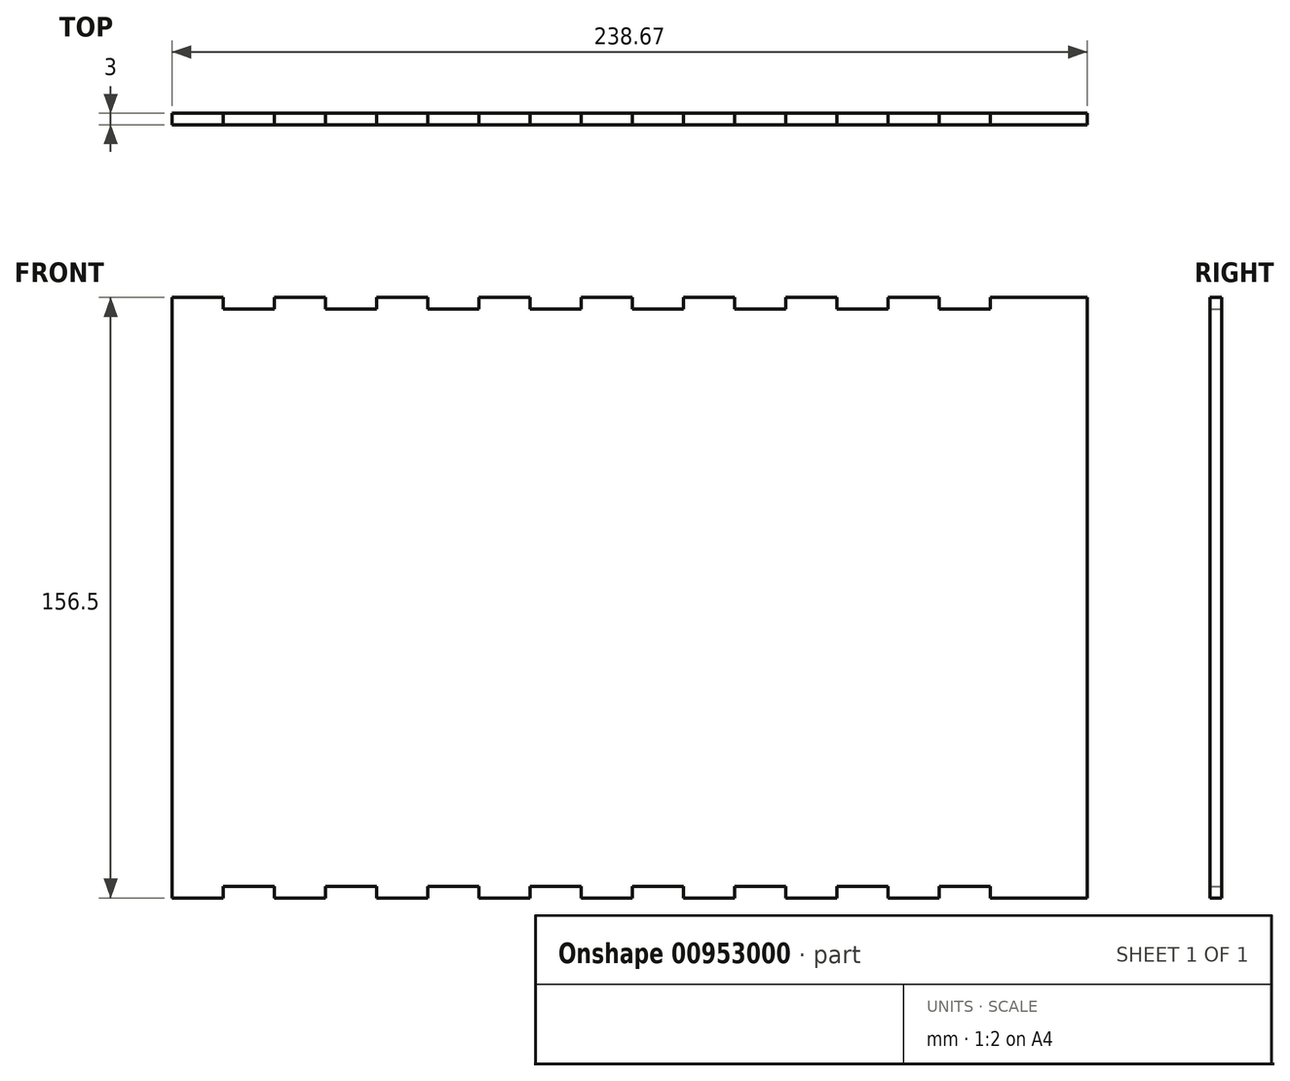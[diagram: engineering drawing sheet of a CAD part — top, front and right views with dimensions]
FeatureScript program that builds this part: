
annotation { "Feature Type Name" : "Feature", "Feature Type Description" : "" }
export const myFeature = defineFeature(function(context is Context, id is Id, definition is map)
    precondition{}
    {
        {
            var Q0;
            Q0=qCreatedBy(makeId("Front.planeOp"),FACE);
            var sketch = newSketch(context, id + "F0", { "sketchPlane" : qUnion([Q0])});
            skPoint(sketch, "E0.middle", {"position": v(-0.98, 0.74) * mm});
            skLineSegment(sketch, "E1", {"start": v(-87.73, 79.24) * mm, "end": v(-74.4, 79.24) * mm});
            skLineSegment(sketch, "E2", {"start": v(-87.73, 82.24) * mm, "end": v(-87.73, 79.24) * mm});
            skLineSegment(sketch, "E3", {"start": v(-74.4, 82.24) * mm, "end": v(-74.4, 79.24) * mm});
            skLineSegment(sketch, "E4", {"start": v(-61.06, 82.24) * mm, "end": v(-61.06, 79.24) * mm});
            skLineSegment(sketch, "E5", {"start": v(-47.73, 82.24) * mm, "end": v(-47.73, 79.24) * mm});
            skLineSegment(sketch, "E6", {"start": v(-34.4, 82.24) * mm, "end": v(-34.4, 79.24) * mm});
            skLineSegment(sketch, "E7", {"start": v(-21.06, 82.24) * mm, "end": v(-21.06, 79.24) * mm});
            skLineSegment(sketch, "E8", {"start": v(-7.73, 82.24) * mm, "end": v(-7.73, 79.24) * mm});
            skLineSegment(sketch, "E9", {"start": v(5.6, 82.24) * mm, "end": v(5.6, 79.24) * mm});
            skLineSegment(sketch, "E10", {"start": v(18.94, 82.24) * mm, "end": v(18.94, 79.24) * mm});
            skLineSegment(sketch, "E11", {"start": v(32.27, 82.24) * mm, "end": v(32.27, 79.24) * mm});
            skLineSegment(sketch, "E12", {"start": v(45.6, 82.24) * mm, "end": v(45.6, 79.24) * mm});
            skLineSegment(sketch, "E13", {"start": v(58.94, 82.24) * mm, "end": v(58.94, 79.24) * mm});
            skLineSegment(sketch, "E14", {"start": v(72.27, 82.24) * mm, "end": v(72.27, 79.24) * mm});
            skLineSegment(sketch, "E15", {"start": v(85.6, 82.24) * mm, "end": v(85.6, 79.24) * mm});
            skLineSegment(sketch, "E16.trimOffspring", {"start": v(-87.73, 82.24) * mm, "end": v(-101.06, 82.24) * mm});
            skLineSegment(sketch, "E17.trimOffspring", {"start": v(-61.06, 79.24) * mm, "end": v(-47.73, 79.24) * mm});
            skLineSegment(sketch, "E18.trimOffspring", {"start": v(-61.06, 82.24) * mm, "end": v(-74.4, 82.24) * mm});
            skLineSegment(sketch, "E19.trimOffspring", {"start": v(-34.4, 79.24) * mm, "end": v(-21.06, 79.24) * mm});
            skLineSegment(sketch, "E20.trimOffspring", {"start": v(-34.4, 82.24) * mm, "end": v(-47.73, 82.24) * mm});
            skLineSegment(sketch, "E21.trimOffspring", {"start": v(-7.73, 79.24) * mm, "end": v(5.6, 79.24) * mm});
            skLineSegment(sketch, "E22.trimOffspring", {"start": v(-7.73, 82.24) * mm, "end": v(-21.06, 82.24) * mm});
            skLineSegment(sketch, "E23.trimOffspring", {"start": v(18.94, 79.24) * mm, "end": v(32.27, 79.24) * mm});
            skLineSegment(sketch, "E24.trimOffspring", {"start": v(18.94, 82.24) * mm, "end": v(5.6, 82.24) * mm});
            skLineSegment(sketch, "E25.trimOffspring", {"start": v(45.6, 79.24) * mm, "end": v(58.94, 79.24) * mm});
            skLineSegment(sketch, "E26.trimOffspring", {"start": v(45.6, 82.24) * mm, "end": v(32.27, 82.24) * mm});
            skLineSegment(sketch, "E27.trimOffspring", {"start": v(72.27, 79.24) * mm, "end": v(85.6, 79.24) * mm});
            skLineSegment(sketch, "E28.trimOffspring", {"start": v(72.27, 82.24) * mm, "end": v(58.94, 82.24) * mm});
            skLineSegment(sketch, "E29", {"start": v(85.6, 82.24) * mm, "end": v(110.94, 82.24) * mm});
            skLineSegment(sketch, "E30", {"start": v(-114.4, 79.24) * mm, "end": v(-101.06, 79.24) * mm});
            skLineSegment(sketch, "E31", {"start": v(-114.4, 82.24) * mm, "end": v(-114.4, 79.24) * mm});
            skLineSegment(sketch, "E32.trimOffspring", {"start": v(-114.4, 82.24) * mm, "end": v(-127.73, 82.24) * mm});
            skLineSegment(sketch, "E33.MirrorCS", {"start": v(-114.4, -74.26) * mm, "end": v(-114.4, -71.26) * mm});
            skLineSegment(sketch, "E34.MirrorCS", {"start": v(-101.06, -74.26) * mm, "end": v(-101.06, -71.26) * mm});
            skLineSegment(sketch, "E35.MirrorCS", {"start": v(-61.06, -74.26) * mm, "end": v(-61.06, -71.26) * mm});
            skLineSegment(sketch, "E36.MirrorCS", {"start": v(32.27, -74.26) * mm, "end": v(32.27, -71.26) * mm});
            skLineSegment(sketch, "E37.MirrorCS", {"start": v(-74.4, -74.26) * mm, "end": v(-74.4, -71.26) * mm});
            skLineSegment(sketch, "E38.MirrorCS", {"start": v(-87.73, -74.26) * mm, "end": v(-87.73, -71.26) * mm});
            skLineSegment(sketch, "E39.MirrorCS", {"start": v(-21.06, -74.26) * mm, "end": v(-21.06, -71.26) * mm});
            skLineSegment(sketch, "E40.MirrorCS", {"start": v(45.6, -74.26) * mm, "end": v(45.6, -71.26) * mm});
            skLineSegment(sketch, "E41.MirrorCS", {"start": v(72.27, -74.26) * mm, "end": v(72.27, -71.26) * mm});
            skLineSegment(sketch, "E42.MirrorCS", {"start": v(85.6, -74.26) * mm, "end": v(85.6, -71.26) * mm});
            skLineSegment(sketch, "E43.MirrorCS", {"start": v(-7.73, -74.26) * mm, "end": v(-7.73, -71.26) * mm});
            skLineSegment(sketch, "E44.MirrorCS", {"start": v(-34.4, -74.26) * mm, "end": v(-34.4, -71.26) * mm});
            skLineSegment(sketch, "E45.MirrorCS", {"start": v(58.94, -74.26) * mm, "end": v(58.94, -71.26) * mm});
            skLineSegment(sketch, "E46.MirrorCS", {"start": v(5.6, -74.26) * mm, "end": v(5.6, -71.26) * mm});
            skLineSegment(sketch, "E47.MirrorCS", {"start": v(-47.73, -74.26) * mm, "end": v(-47.73, -71.26) * mm});
            skLineSegment(sketch, "E48.MirrorCS", {"start": v(18.94, -74.26) * mm, "end": v(18.94, -71.26) * mm});
            skLineSegment(sketch, "E49.MirrorCS", {"start": v(-114.4, -74.26) * mm, "end": v(-127.73, -74.26) * mm});
            skLineSegment(sketch, "E50.MirrorCS", {"start": v(-114.4, -71.26) * mm, "end": v(-101.06, -71.26) * mm});
            skLineSegment(sketch, "E51.MirrorCS", {"start": v(-7.73, -71.26) * mm, "end": v(5.6, -71.26) * mm});
            skLineSegment(sketch, "E52.MirrorCS", {"start": v(45.6, -74.26) * mm, "end": v(32.27, -74.26) * mm});
            skLineSegment(sketch, "E53.MirrorCS", {"start": v(72.27, -71.26) * mm, "end": v(85.6, -71.26) * mm});
            skLineSegment(sketch, "E54.MirrorCS", {"start": v(85.6, -74.26) * mm, "end": v(110.94, -74.26) * mm});
            skLineSegment(sketch, "E55.MirrorCS", {"start": v(-7.73, -74.26) * mm, "end": v(-21.06, -74.26) * mm});
            skLineSegment(sketch, "E56.MirrorCS", {"start": v(72.27, -74.26) * mm, "end": v(58.94, -74.26) * mm});
            skLineSegment(sketch, "E57.MirrorCS", {"start": v(-34.4, -74.26) * mm, "end": v(-47.73, -74.26) * mm});
            skLineSegment(sketch, "E58.MirrorCS", {"start": v(-61.06, -71.26) * mm, "end": v(-47.73, -71.26) * mm});
            skLineSegment(sketch, "E59.MirrorCS", {"start": v(18.94, -74.26) * mm, "end": v(5.6, -74.26) * mm});
            skLineSegment(sketch, "E60.MirrorCS", {"start": v(-34.4, -71.26) * mm, "end": v(-21.06, -71.26) * mm});
            skLineSegment(sketch, "E61.MirrorCS", {"start": v(-87.73, -71.26) * mm, "end": v(-74.4, -71.26) * mm});
            skLineSegment(sketch, "E62.MirrorCS", {"start": v(18.94, -71.26) * mm, "end": v(32.27, -71.26) * mm});
            skLineSegment(sketch, "E63.MirrorCS", {"start": v(45.6, -71.26) * mm, "end": v(58.94, -71.26) * mm});
            skLineSegment(sketch, "E64.MirrorCS", {"start": v(-87.73, -74.26) * mm, "end": v(-101.06, -74.26) * mm});
            skLineSegment(sketch, "E65.MirrorCS", {"start": v(-61.06, -74.26) * mm, "end": v(-74.4, -74.26) * mm});
            skLineSegment(sketch, "E66", {"start": v(110.94, 82.24) * mm, "end": v(110.94, -74.26) * mm});
            skLineSegment(sketch, "E67", {"start": v(-101.06, 82.24) * mm, "end": v(-101.06, 79.24) * mm});
            skLineSegment(sketch, "E68", {"start": v(-127.73, -74.26) * mm, "end": v(-127.73, 82.24) * mm});
            skSolve(sketch);
        }
        {
            var Q0;
            Q0=makeQuery(id+"F0.imprint","IMPRINT",FACE,{"disambiguationData":[TD([[makeQuery(id+"F0.imprint","IMPRINT",EDGE,{"derivedFrom":sQuery(id+"F0.wireOp",EDGE,"E1")}),-1.0]])]});
            extrude(context, id + "F1", {"entities" : qUnion([Q0]), "depth" : 3 * mm, "offsetDistance" : 25 * mm});
        }
    });
